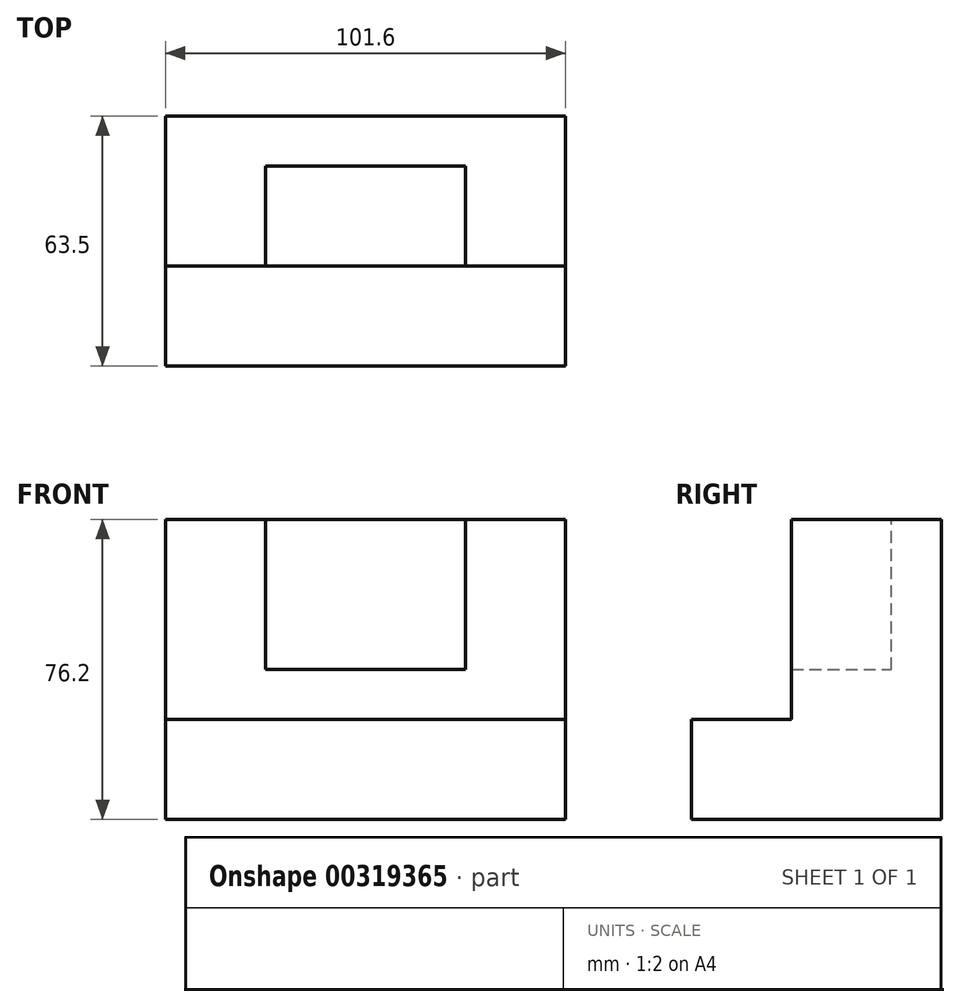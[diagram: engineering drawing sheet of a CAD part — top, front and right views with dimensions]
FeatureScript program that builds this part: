
annotation { "Feature Type Name" : "Feature", "Feature Type Description" : "" }
export const myFeature = defineFeature(function(context is Context, id is Id, definition is map)
    precondition{}
    {
        {
            var Q0;
            Q0=qCreatedBy(makeId("Right.planeOp"),FACE);
            var sketch = newSketch(context, id + "F0", { "sketchPlane" : qUnion([Q0])});
            skLineSegment(sketch, "E0", {"start": v(-44.45, -42.95) * mm, "end": v(19.05, -42.95) * mm});
            skLineSegment(sketch, "E1", {"start": v(19.05, -42.95) * mm, "end": v(19.05, 33.25) * mm});
            skLineSegment(sketch, "E2", {"start": v(19.05, 33.25) * mm, "end": v(-19.05, 33.25) * mm});
            skLineSegment(sketch, "E3", {"start": v(-19.05, 33.25) * mm, "end": v(-19.05, -17.55) * mm});
            skLineSegment(sketch, "E4", {"start": v(-19.05, -17.55) * mm, "end": v(-44.45, -17.55) * mm});
            skLineSegment(sketch, "E5", {"start": v(-44.45, -17.55) * mm, "end": v(-44.45, -42.95) * mm});
            skSolve(sketch);
        }
        {
            var Q0;
            Q0=makeQuery(id+"F0.imprint","IMPRINT",FACE,{"disambiguationData":[TD([[makeQuery(id+"F0.imprint","IMPRINT",EDGE,{"derivedFrom":sQuery(id+"F0.wireOp",EDGE,"E0")}),1.0]])]});
            extrude(context, id + "F1", {"entities" : qUnion([Q0]), "depth" : 101.6 * mm});
        }
        {
            var Q0;
            Q0=makeQuery(id+"F1.opExtrude","SWEPT_FACE",FACE,{"disambiguationData":[OSD([sQuery(id+"F0.wireOp",EDGE,"E2")])]});
            var sketch = newSketch(context, id + "F2", { "sketchPlane" : qUnion([Q0])});
            skLineSegment(sketch, "E6", {"start": v(76.2, -19.05) * mm, "end": v(25.4, -19.05) * mm});
            skLineSegment(sketch, "E7", {"start": v(25.4, -19.05) * mm, "end": v(25.4, 6.35) * mm});
            skLineSegment(sketch, "E8", {"start": v(25.4, 6.35) * mm, "end": v(76.2, 6.35) * mm});
            skLineSegment(sketch, "E9", {"start": v(76.2, 6.35) * mm, "end": v(76.2, -19.05) * mm});
            skSolve(sketch);
        }
        {
            var Q0;
            Q0=makeQuery(id+"F2.imprint","IMPRINT",FACE,{"disambiguationData":[TD([[makeQuery(id+"F2.imprint","IMPRINT",EDGE,{"derivedFrom":sQuery(id+"F2.wireOp",EDGE,"E6")}),-1.0]])]});
            extrude(context, id + "F3", {"entities" : qUnion([Q0]), "operationType" : NewBodyOperationType.REMOVE, "oppositeDirection" : true, "depth" : 38.1 * mm});
        }
    });
